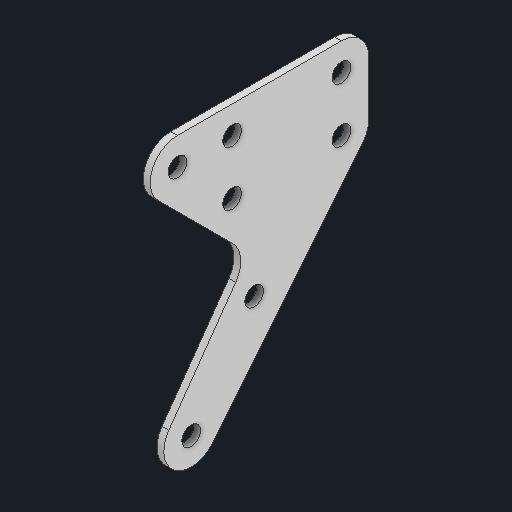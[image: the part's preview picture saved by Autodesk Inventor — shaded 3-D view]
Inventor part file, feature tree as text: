
AUTODESK INVENTOR PART (.ipt)
format: ipt  version: 2025 (Build 290162000, 162)  size: 131,072 bytes
history: native  units: in
note: dims shown in document units (in); Inventor stores cm internally (conversion verified against a paired STEP export)
features: other x5, sketch x1
ambient origin geometry x8: Origin, YZ Plane, XZ Plane, XY Plane, X Axis, Y Axis, Z Axis, Center Point
bodies: Solid1 (feature_tree)
feature tree (6):
  other  "triangle_brace_gusset.ipt"
  other  "Blocks"
  other  "maiin"
  other  "Solid1::triangle_brace_gusset.ipt"
  other  "TaggingFeature1"
  sketch  "Sketch1"  dims[d0=0.3937in d1=0.5in d4=0.25in d6=0.172in]
